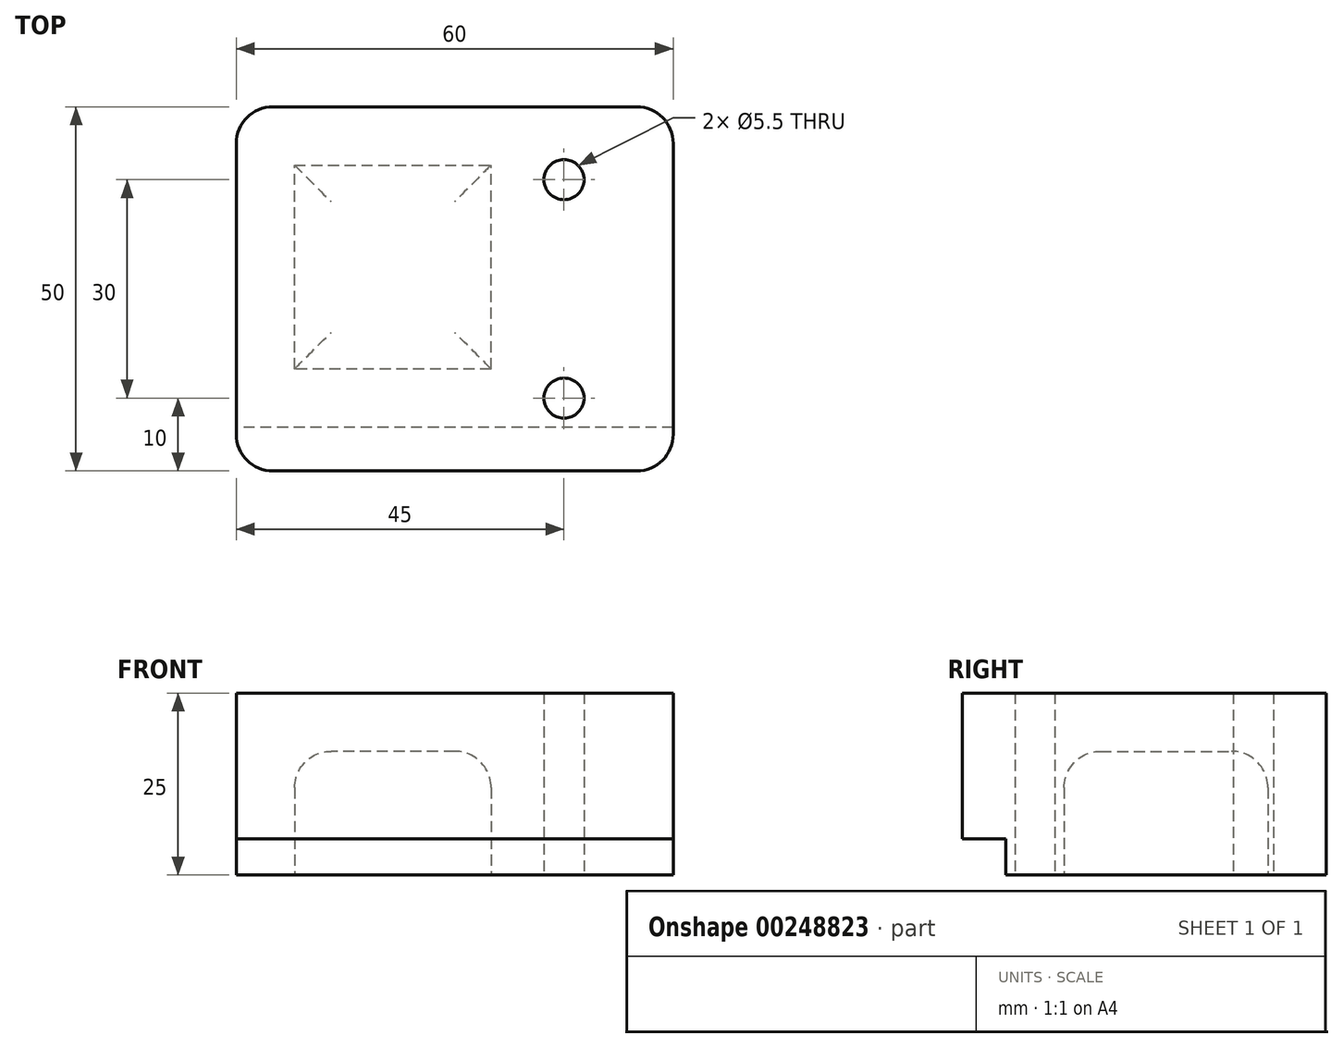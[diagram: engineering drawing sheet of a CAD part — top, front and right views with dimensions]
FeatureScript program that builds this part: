
annotation { "Feature Type Name" : "Feature", "Feature Type Description" : "" }
export const myFeature = defineFeature(function(context is Context, id is Id, definition is map)
    precondition{}
    {
        {
            var Q0;
            Q0=qCreatedBy(makeId("Top.planeOp"),FACE);
            var sketch = newSketch(context, id + "F0", { "sketchPlane" : qUnion([Q0])});
            skLineSegment(sketch, "E0.bottom", {"start": v(30, 25) * mm, "end": v(-30, 25) * mm});
            skLineSegment(sketch, "E0.top", {"start": v(30, -25) * mm, "end": v(-30, -25) * mm});
            skLineSegment(sketch, "E0.left", {"start": v(30, 25) * mm, "end": v(30, -25) * mm});
            skLineSegment(sketch, "E0.right", {"start": v(-30, 25) * mm, "end": v(-30, -25) * mm});
            skPoint(sketch, "E0.middle", {"position": v(0, 0) * mm});
            skCircle(sketch, "E1", {"center": v(15, 15) * mm, "radius": 2.75 * mm});
            skCircle(sketch, "E2.MirrorC", {"center": v(15, -15) * mm, "radius": 2.75 * mm});
            skSolve(sketch);
        }
        {
            var Q0;
            Q0=makeQuery(id+"F0.imprint","IMPRINT",FACE,{"disambiguationData":[TD([[makeQuery(id+"F0.imprint","IMPRINT",EDGE,{"derivedFrom":sQuery(id+"F0.wireOp",EDGE,"E0.bottom")}),1.0]])]});
            extrude(context, id + "F1", {"entities" : qUnion([Q0]), "depth" : 25 * mm});
        }
        {
            var Q0;
            Q0=makeQuery(id+"F1.opExtrude","SWEPT_FACE",FACE,{"disambiguationData":[OSD([sQuery(id+"F0.wireOp",EDGE,"E0.top")])]});
            var sketch = newSketch(context, id + "F2", { "sketchPlane" : qUnion([Q0])});
            skLineSegment(sketch, "E3", {"start": v(-30, 5) * mm, "end": v(30, 5) * mm});
            skSolve(sketch);
        }
        {
            var Q0;
            {var subQ0=sQuery(id+"F2.wireOp",EDGE,"E3");Q0=makeQuery(id+"F2.imprint","IMPRINT",FACE,{"disambiguationData":[TD([[makeQuery(id+"F2.imprint","IMPRINT",EDGE,{"derivedFrom":subQ0}),-1.0]])]});}
            extrude(context, id + "F3", {"entities" : qUnion([Q0]), "operationType" : NewBodyOperationType.REMOVE, "oppositeDirection" : true, "depth" : 6 * mm});
        }
        {
            var Q0;
            Q0=makeQuery(id+"F1.opExtrude","SWEPT_EDGE",EDGE,{"disambiguationData":[OSD([sQuery(id+"F0.wireOp",EDGE,"E0.top"),sQuery(id+"F0.wireOp",EDGE,"E0.left")])]});
            var Q1;
            Q1=makeQuery(id+"F1.opExtrude","SWEPT_EDGE",EDGE,{"disambiguationData":[OSD([sQuery(id+"F0.wireOp",EDGE,"E0.top"),sQuery(id+"F0.wireOp",EDGE,"E0.right")])]});
            var Q2;
            Q2=makeQuery(id+"F1.opExtrude","SWEPT_EDGE",EDGE,{"disambiguationData":[OSD([sQuery(id+"F0.wireOp",EDGE,"E0.bottom"),sQuery(id+"F0.wireOp",EDGE,"E0.right")])]});
            var Q3;
            Q3=makeQuery(id+"F1.opExtrude","SWEPT_EDGE",EDGE,{"disambiguationData":[OSD([sQuery(id+"F0.wireOp",EDGE,"E0.bottom"),sQuery(id+"F0.wireOp",EDGE,"E0.left")])]});
            fillet(context, id + "F4", {"entities" : qUnion([Q0, Q1, Q2, Q3]), "radius" : 5 * mm, "tangentPropagation" : true, "allowEdgeOverflow" : false});
        }
        {
            var Q0;
            Q0=makeQuery(id+"F1.opExtrude","CAP_FACE",FACE,{"disambiguationData":[OSD([sQuery(id+"F0.wireOp",EDGE,"E0.bottom"),sQuery(id+"F0.wireOp",EDGE,"E0.top"),sQuery(id+"F0.wireOp",EDGE,"E0.left"),sQuery(id+"F0.wireOp",EDGE,"E0.right"),sQuery(id+"F0.wireOp",EDGE,"E1"),sQuery(id+"F0.wireOp",EDGE,"E2.MirrorC")])],"isStart":true});
            var sketch = newSketch(context, id + "F5", { "sketchPlane" : qUnion([Q0])});
            skLineSegment(sketch, "E4", {"start": v(5, 19) * mm, "end": v(5, -25) * mm});
            skLineSegment(sketch, "E5", {"start": v(5, 11) * mm, "end": v(-22, 11) * mm});
            skLineSegment(sketch, "E6", {"start": v(-22, 11) * mm, "end": v(-22, -17) * mm});
            skLineSegment(sketch, "E7", {"start": v(-22, -17) * mm, "end": v(5, -17) * mm});
            skSolve(sketch);
        }
        {
            var Q0;
            {var subQ0=sQuery(id+"F5.wireOp",EDGE,"E5");Q0=makeQuery(id+"F5.imprint","IMPRINT",FACE,{"disambiguationData":[TD([[makeQuery(id+"F5.imprint","IMPRINT",EDGE,{"derivedFrom":subQ0}),1.0]])]});}
            extrude(context, id + "F6", {"entities" : qUnion([Q0]), "operationType" : NewBodyOperationType.REMOVE, "oppositeDirection" : true, "depth" : (25 - 8) * mm});
        }
        {
            var Q0;
            Q0=makeQuery(id+"F6.boolean.opBoolean","COPY",EDGE,{"derivedFrom":makeQuery(id+"F6.opExtrude","CAP_EDGE",EDGE,{"disambiguationData":[OSD([sQuery(id+"F5.wireOp",EDGE,"E5")])],"isStart":false})});
            var Q1;
            Q1=makeQuery(id+"F6.boolean.opBoolean","COPY",EDGE,{"derivedFrom":makeQuery(id+"F6.opExtrude","CAP_EDGE",EDGE,{"disambiguationData":[OSD([sQuery(id+"F5.wireOp",EDGE,"E4")])],"isStart":false})});
            var Q2;
            Q2=makeQuery(id+"F6.boolean.opBoolean","COPY",EDGE,{"derivedFrom":makeQuery(id+"F6.opExtrude","CAP_EDGE",EDGE,{"disambiguationData":[OSD([sQuery(id+"F5.wireOp",EDGE,"E7")])],"isStart":false})});
            var Q3;
            Q3=makeQuery(id+"F6.boolean.opBoolean","COPY",EDGE,{"derivedFrom":makeQuery(id+"F6.opExtrude","CAP_EDGE",EDGE,{"disambiguationData":[OSD([sQuery(id+"F5.wireOp",EDGE,"E6")])],"isStart":false})});
            fillet(context, id + "F7", {"entities" : qUnion([Q0, Q1, Q2, Q3]), "radius" : 5 * mm, "tangentPropagation" : true, "allowEdgeOverflow" : false});
        }
    });
